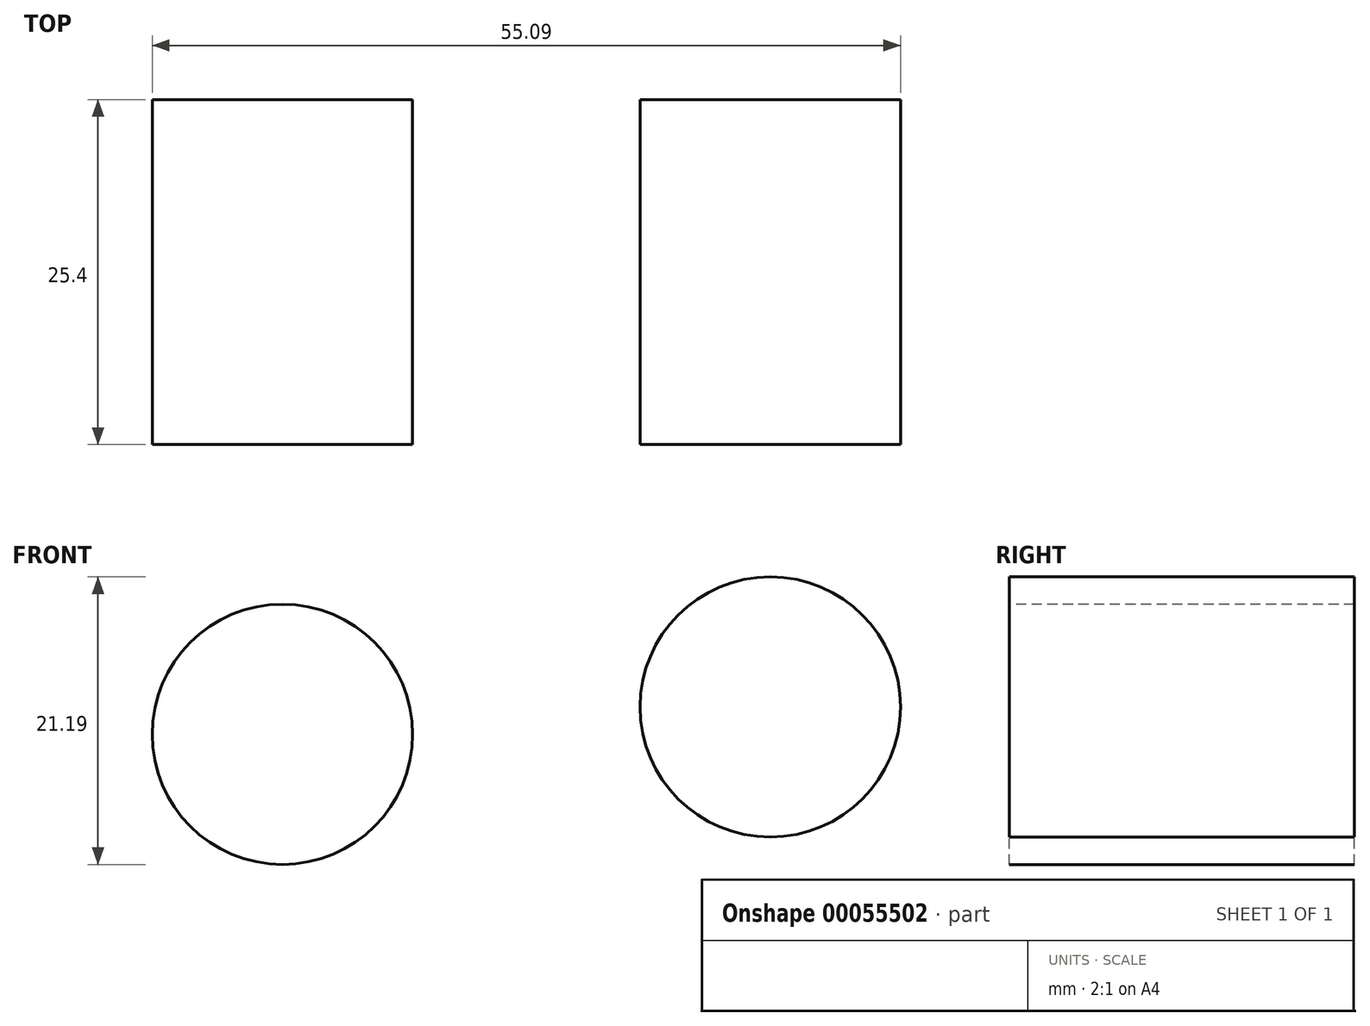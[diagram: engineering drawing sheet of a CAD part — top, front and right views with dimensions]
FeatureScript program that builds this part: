
annotation { "Feature Type Name" : "Feature", "Feature Type Description" : "" }
export const myFeature = defineFeature(function(context is Context, id is Id, definition is map)
    precondition{}
    {
        {
            var Q0;
            Q0=qCreatedBy(makeId("Front.planeOp"),FACE);
            var sketch = newSketch(context, id + "F0", { "sketchPlane" : qUnion([Q0])});
            skLineSegment(sketch, "E0.bottom", {"start": v(0, 0) * mm, "end": v(72.85, 0) * mm});
            skLineSegment(sketch, "E0.top", {"start": v(0, 43.49) * mm, "end": v(72.85, 43.49) * mm});
            skLineSegment(sketch, "E0.left", {"start": v(0, 0) * mm, "end": v(0, 43.49) * mm});
            skLineSegment(sketch, "E0.right", {"start": v(72.85, 0) * mm, "end": v(72.85, 43.49) * mm});
            skCircle(sketch, "E1", {"center": v(12.71, 11) * mm, "radius": 9.59 * mm});
            skCircle(sketch, "E2", {"center": v(48.63, 13.02) * mm, "radius": 9.59 * mm});
            skSolve(sketch);
        }
        {
            var Q0;
            Q0=makeQuery(id+"F0.imprint","IMPRINT",FACE,{"disambiguationData":[TD([[makeQuery(id+"F0.imprint","IMPRINT",EDGE,{"derivedFrom":sQuery(id+"F0.wireOp",EDGE,"E1")}),1.0]])]});
            var Q1;
            Q1=makeQuery(id+"F0.imprint","IMPRINT",FACE,{"disambiguationData":[TD([[makeQuery(id+"F0.imprint","IMPRINT",EDGE,{"derivedFrom":sQuery(id+"F0.wireOp",EDGE,"E2")}),1.0]])]});
            extrude(context, id + "F1", {"entities" : qUnion([Q0, Q1]), "oppositeDirection" : true, "depth" : 25.4 * mm});
        }
    });
